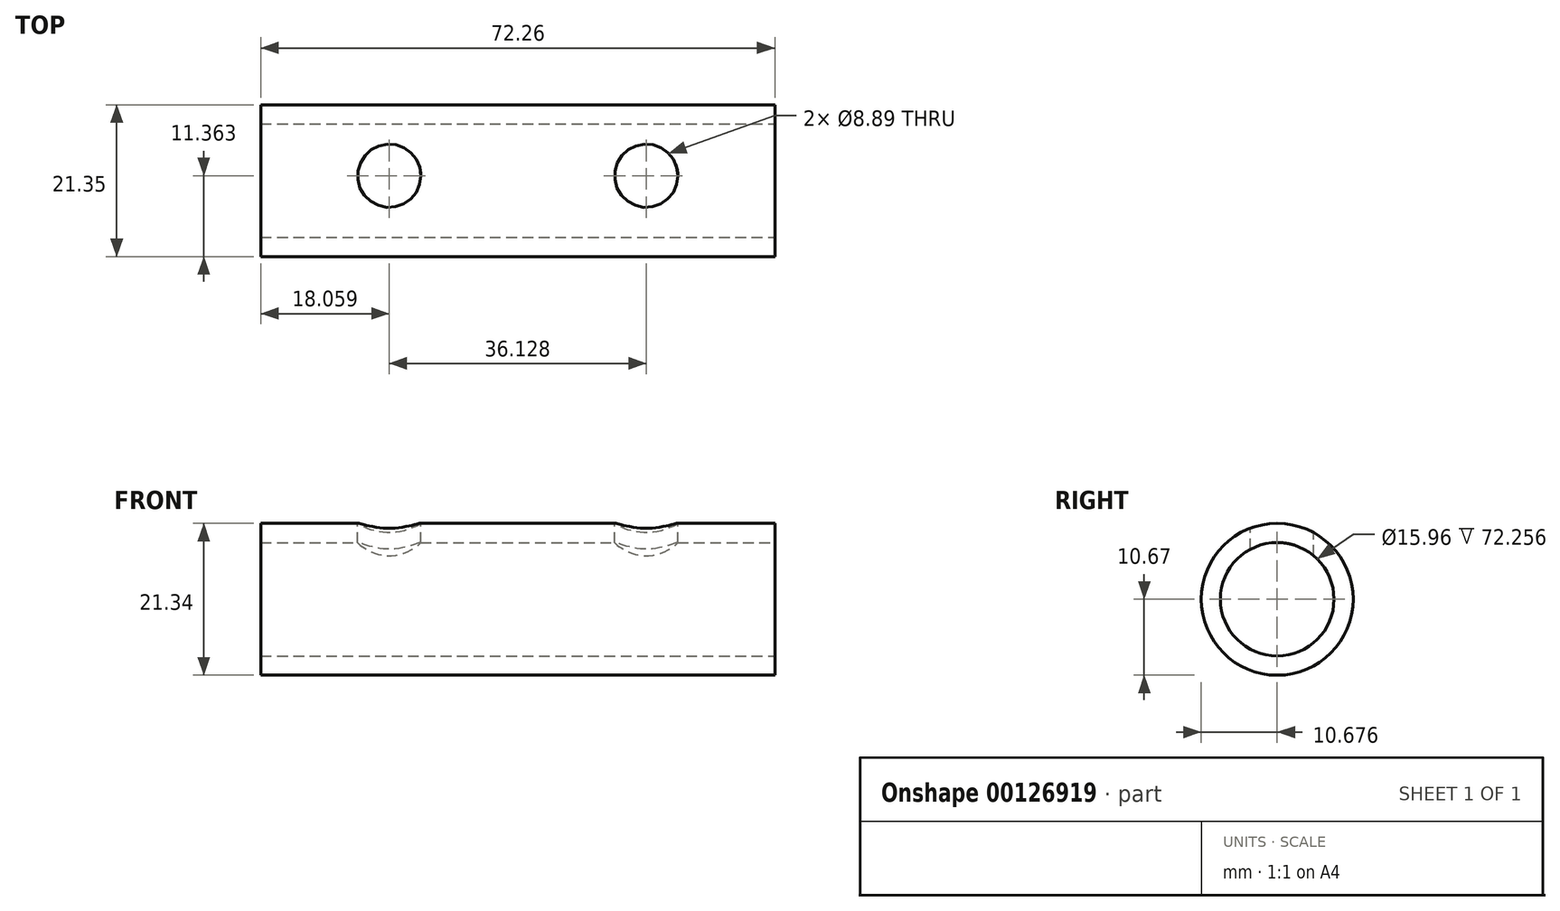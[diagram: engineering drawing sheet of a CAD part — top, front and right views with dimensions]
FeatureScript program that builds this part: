
annotation { "Feature Type Name" : "Feature", "Feature Type Description" : "" }
export const myFeature = defineFeature(function(context is Context, id is Id, definition is map)
    precondition{}
    {
        {
            var Q0;
            Q0=qCreatedBy(makeId("Right.planeOp"),FACE);
            var sketch = newSketch(context, id + "F0", { "sketchPlane" : qUnion([Q0])});
            skLineSegment(sketch, "E0.bottom", {"start": v(-20.7, -21.76) * mm, "end": v(-46.1, -21.76) * mm});
            skLineSegment(sketch, "E0.top", {"start": v(-20.7, -47.16) * mm, "end": v(-46.1, -47.16) * mm});
            skLineSegment(sketch, "E0.left", {"start": v(-20.7, -21.76) * mm, "end": v(-20.7, -47.16) * mm});
            skLineSegment(sketch, "E0.right", {"start": v(-46.1, -21.76) * mm, "end": v(-46.1, -47.16) * mm});
            skPoint(sketch, "E1.right.end.orphan", {"position": v(-20.7, 0) * mm});
            skSolve(sketch);
        }
        {
            var Q0;
            Q0=makeQuery(id+"F0.imprint","IMPRINT",FACE,{"disambiguationData":[TD([[makeQuery(id+"F0.imprint","IMPRINT",EDGE,{"derivedFrom":sQuery(id+"F0.wireOp",EDGE,"E0.bottom")}),1.0]])]});
            extrude(context, id + "F1", {"entities" : qUnion([Q0]), "depth" : 72.26 * mm});
        }
        {
            var Q0;
            Q0=makeQuery(id+"F1.opExtrude","CAP_FACE",FACE,{"disambiguationData":[OSD([sQuery(id+"F0.wireOp",EDGE,"E0.bottom"),sQuery(id+"F0.wireOp",EDGE,"E0.top"),sQuery(id+"F0.wireOp",EDGE,"E0.left"),sQuery(id+"F0.wireOp",EDGE,"E0.right")])],"isStart":false});
            var sketch = newSketch(context, id + "F2", { "sketchPlane" : qUnion([Q0])});
            skCircle(sketch, "E2", {"center": v(-34.1, -34.62) * mm, "radius": 10.67 * mm});
            skCircle(sketch, "E3", {"center": v(-34.1, -34.62) * mm, "radius": 7.98 * mm});
            skSolve(sketch);
        }
        {
            var Q0;
            Q0=makeQuery(id+"F2.imprint","IMPRINT",FACE,{"disambiguationData":[TD([[makeQuery(id+"F2.imprint","IMPRINT",EDGE,{"derivedFrom":sQuery(id+"F2.wireOp",EDGE,"E3")}),1.0]])]});
            extrude(context, id + "F3", {"entities" : qUnion([Q0]), "operationType" : NewBodyOperationType.REMOVE, "oppositeDirection" : true, "depth" : 82.87 * mm});
        }
        {
            var Q0;
            Q0=makeQuery(id+"F1.opExtrude","SWEPT_FACE",FACE,{"disambiguationData":[OSD([sQuery(id+"F0.wireOp",EDGE,"E0.bottom")])]});
            var sketch = newSketch(context, id + "F4", { "sketchPlane" : qUnion([Q0])});
            skLineSegment(sketch, "E4", {"start": v(36.13, -46.1) * mm, "end": v(36.13, -20.7) * mm});
            skPoint(sketch, "E5", {"position": v(18.06, -33.4) * mm});
            skPoint(sketch, "E5.positionSnap0", {"position": v(36.13, -33.4) * mm});
            skPoint(sketch, "E6", {"position": v(54.19, -33.4) * mm});
            skSolve(sketch);
        }
        {
            var Q0;
            Q0=sQuery(id+"F4.wireOp",VERTEX,"E5");
            var Q1;
            Q1=sQuery(id+"F4.wireOp",VERTEX,"E6");
            var Q2;
            Q2=makeQuery(id+"F1.opExtrude","SWEPT_BODY",BODY,{"disambiguationData":[OSD([sQuery(id+"F0.wireOp",EDGE,"E0.bottom"),sQuery(id+"F0.wireOp",EDGE,"E0.top"),sQuery(id+"F0.wireOp",EDGE,"E0.left"),sQuery(id+"F0.wireOp",EDGE,"E0.right")])]});
            hole(context, id + "F5", {"style" : HoleStyle.SIMPLE, "endStyle" : HoleEndStyle.BLIND, "holeDiameter" : 8.9 * mm, "holeDepth" : 12.7 * mm, "locations" : qUnion([Q0, Q1]), "scope" : qUnion([Q2])});
        }
        {
            var Q0;
            Q0=makeQuery(id+"F2.imprint","IMPRINT",FACE,{"disambiguationData":[TD([[makeQuery(id+"F2.imprint","IMPRINT",EDGE,{"derivedFrom":sQuery(id+"F2.wireOp",EDGE,"E2")}),-1.0]])]});
            extrude(context, id + "F6", {"entities" : qUnion([Q0]), "operationType" : NewBodyOperationType.REMOVE, "oppositeDirection" : true, "depth" : 88.86 * mm});
        }
    });
